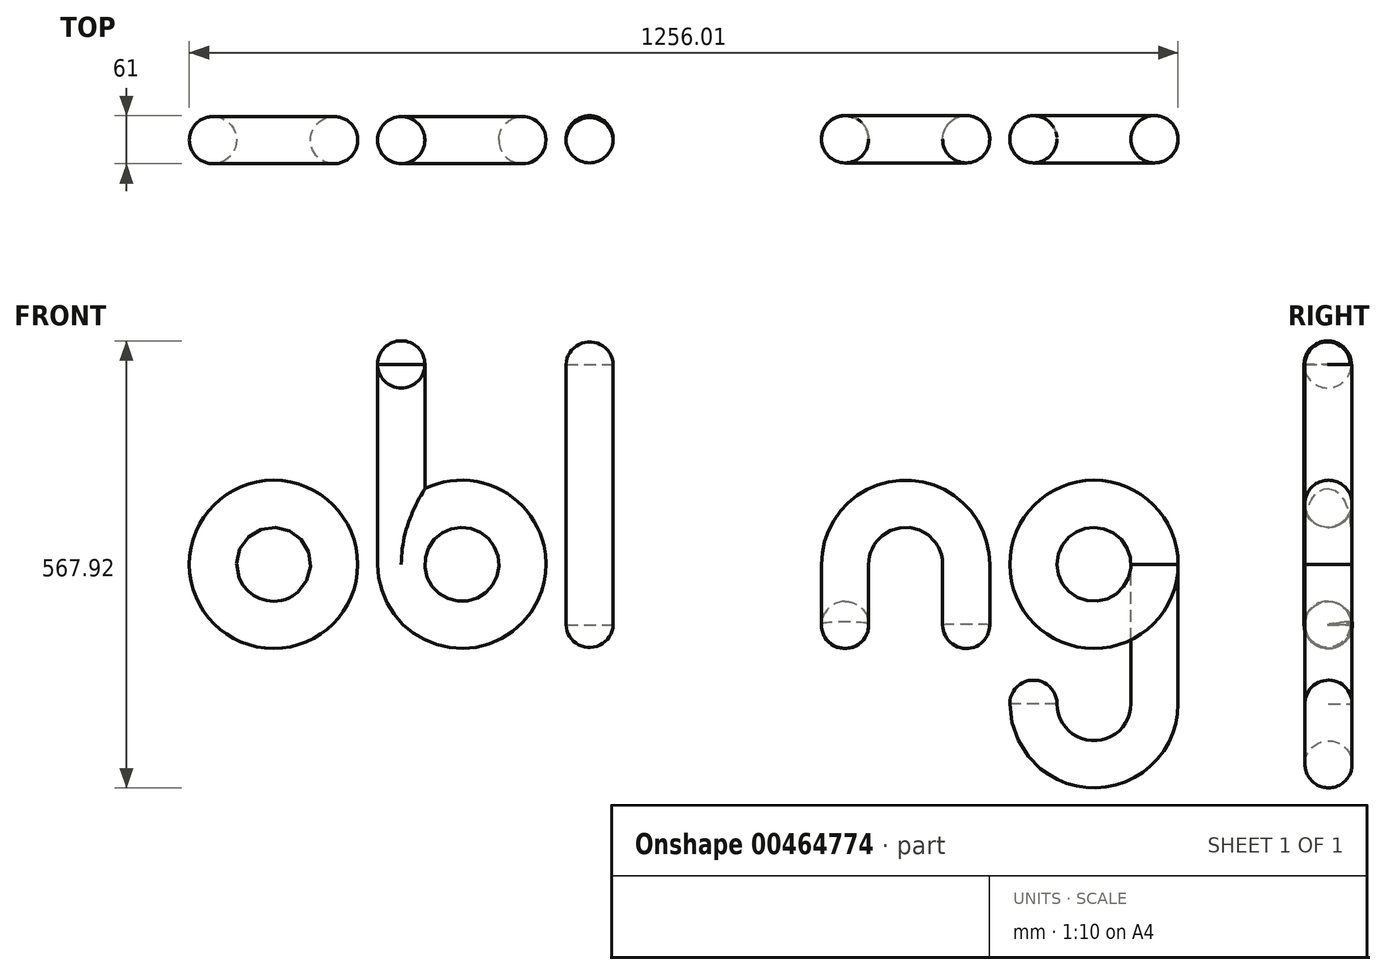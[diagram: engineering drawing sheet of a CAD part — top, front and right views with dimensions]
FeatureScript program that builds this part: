
annotation { "Feature Type Name" : "Feature", "Feature Type Description" : "" }
export const myFeature = defineFeature(function(context is Context, id is Id, definition is map)
    precondition{}
    {
        {
            var Q0;
            Q0=qCreatedBy(makeId("Top.planeOp"),FACE);
            var sketch = newSketch(context, id + "F0", { "sketchPlane" : qUnion([Q0])});
            skCircle(sketch, "E0", {"center": v(0, 0) * mm, "radius": 29.96 * mm});
            skLineSegment(sketch, "E1", {"start": v(-39.68, 0) * mm, "end": v(42.5, 0) * mm});
            skSolve(sketch);
        }
        {
            var Q0;
            {var subQ0=sQuery(id+"F0.wireOp",EDGE,"E1");var subQ1=sQuery(id+"F0.wireOp",EDGE,"E0");var subQ2=makeQuery(id+"F0.imprint","INTERSECT",VERTEX,{"disambiguationData":[OD(0.0)],"derivedFrom":[subQ1,subQ0]});Q0=makeQuery(id+"F0.imprint","IMPRINT",FACE,{"disambiguationData":[TD([[makeQuery(id+"F0.imprint","IMPRINT",EDGE,{"disambiguationData":[TD([[subQ2,1.0]])],"derivedFrom":subQ1}),1.0]])]});}
            var Q1;
            Q1=sQuery(id+"F0.wireOp",EDGE,"E1");
            revolve(context, id + "F1", {"entities" : qUnion([Q0]), "axis" : qUnion([Q1]), "revolveType" : RevolveType.FULL});
        }
        {
            var Q0;
            {var subQ0=sQuery(id+"F0.wireOp",EDGE,"E1");var subQ1=sQuery(id+"F0.wireOp",EDGE,"E0");var subQ2=makeQuery(id+"F0.imprint","INTERSECT",VERTEX,{"disambiguationData":[OD(0.0)],"derivedFrom":[subQ1,subQ0]});Q0=makeQuery(id+"F0.imprint","IMPRINT",FACE,{"disambiguationData":[TD([[makeQuery(id+"F0.imprint","IMPRINT",EDGE,{"disambiguationData":[TD([[subQ2,1.0]])],"derivedFrom":subQ1}),1.0]])]});}
            var Q1;
            {var subQ0=sQuery(id+"F0.wireOp",EDGE,"E1");var subQ1=sQuery(id+"F0.wireOp",EDGE,"E0");var subQ2=makeQuery(id+"F0.imprint","INTERSECT",VERTEX,{"disambiguationData":[OD(0.0)],"derivedFrom":[subQ1,subQ0]});Q1=makeQuery(id+"F0.imprint","IMPRINT",FACE,{"disambiguationData":[TD([[makeQuery(id+"F0.imprint","IMPRINT",EDGE,{"disambiguationData":[TD([[subQ2,-1.0]])],"derivedFrom":subQ1}),1.0]])]});}
            extrude(context, id + "F2", {"entities" : qUnion([Q0, Q1]), "oppositeDirection" : true, "depth" : 254 * mm});
        }
        {
            var Q0;
            Q0=makeQuery(id+"F2.opExtrude","CAP_FACE",FACE,{"disambiguationData":[OSD([sQuery(id+"F0.wireOp",EDGE,"E0")])],"isStart":false});
            var sketch = newSketch(context, id + "F3", { "sketchPlane" : qUnion([Q0])});
            skLineSegment(sketch, "E2", {"start": v(76.95, 56.53) * mm, "end": v(76.95, -45.65) * mm});
            skLineSegment(sketch, "E3", {"start": v(-42.66, 53.66) * mm, "end": v(-42.66, -48.45) * mm});
            skCircle(sketch, "E4", {"center": v(-85.32, 0) * mm, "radius": 29.96 * mm});
            skLineSegment(sketch, "E5", {"start": v(-162.27, 52.41) * mm, "end": v(-162.27, -53.8) * mm});
            skCircle(sketch, "E6", {"center": v(153.9, 0) * mm, "radius": 29.96 * mm});
            skLineSegment(sketch, "E7", {"start": v(-185.14, -1.07) * mm, "end": v(1029.73, -1.07) * mm});
            skLineSegment(sketch, "E8", {"start": v(196.56, 55.6) * mm, "end": v(196.56, -44.98) * mm});
            skCircle(sketch, "E9", {"center": v(239.22, -1.07) * mm, "radius": 29.96 * mm});
            skLineSegment(sketch, "E10", {"start": v(281.88, 60.27) * mm, "end": v(281.88, -45.7) * mm});
            skCircle(sketch, "E11", {"center": v(324.54, -1.07) * mm, "radius": 29.96 * mm});
            skLineSegment(sketch, "E12", {"start": v(401.5, -44.95) * mm, "end": v(401.5, 59.66) * mm});
            skCircle(sketch, "E13", {"center": v(478.44, -1.07) * mm, "radius": 29.96 * mm});
            skCircle(sketch, "E14", {"center": v(563.76, -1.07) * mm, "radius": 29.96 * mm});
            skCircle(sketch, "E15", {"center": v(717.66, -1.07) * mm, "radius": 29.96 * mm});
            skCircle(sketch, "E16", {"center": v(802.98, -1.07) * mm, "radius": 29.96 * mm});
            skLineSegment(sketch, "E17", {"start": v(521.1, -41.28) * mm, "end": v(521.1, 41.77) * mm});
            skLineSegment(sketch, "E18", {"start": v(640.7, -43.14) * mm, "end": v(640.7, 48.3) * mm});
            skLineSegment(sketch, "E19", {"start": v(760.32, -41.28) * mm, "end": v(760.32, 42.7) * mm});
            skLineSegment(sketch, "E20", {"start": v(879.93, -58.07) * mm, "end": v(879.93, 33.38) * mm});
            skCircle(sketch, "E21", {"center": v(956.87, -1.07) * mm, "radius": 29.96 * mm});
            skSolve(sketch);
        }
        {
            var Q0;
            Q0=makeQuery(id+"F3.imprint","IMPRINT",FACE,{"disambiguationData":[TD([[makeQuery(id+"F3.imprint","IMPRINT",EDGE,{"derivedFrom":makeQuery(id+"F2.opExtrude","CAP_EDGE",EDGE,{"disambiguationData":[OSD([sQuery(id+"F0.wireOp",EDGE,"E0")])],"isStart":false})}),-1.0]])]});
            var Q1;
            Q1=sQuery(id+"F3.wireOp",EDGE,"E2");
            revolve(context, id + "F4", {"operationType" : NewBodyOperationType.ADD, "entities" : qUnion([Q0]), "axis" : qUnion([Q1]), "revolveType" : RevolveType.FULL});
        }
        {
            var Q0;
            Q0=makeQuery(id+"F1.opRevolve","SWEPT_BODY",BODY,{"disambiguationData":[OSD([sQuery(id+"F0.wireOp",EDGE,"E0"),sQuery(id+"F0.wireOp",EDGE,"E1")])]});
            transform(context, id + "F5", {"entities" : qUnion([Q0]), "transformType" : TransformType.COPY});
        }
        {
            var Q0;
            Q0=makeQuery(id+"F5.opPattern","COPY",BODY,{"derivedFrom":makeQuery(id+"F1.opRevolve","SWEPT_BODY",BODY,{"disambiguationData":[OSD([sQuery(id+"F0.wireOp",EDGE,"E0"),sQuery(id+"F0.wireOp",EDGE,"E1")])]}),"instanceName":"1"});
            deleteBodies(context, id + "F6", {"entities" : qUnion([Q0])});
        }
        {
            var Q0;
            Q0=makeQuery(id+"F3.imprint","IMPRINT",FACE,{"disambiguationData":[TD([[makeQuery(id+"F3.imprint","IMPRINT",EDGE,{"derivedFrom":sQuery(id+"F3.wireOp",EDGE,"E4")}),1.0]])]});
            var Q1;
            Q1=sQuery(id+"F3.wireOp",EDGE,"E5");
            revolve(context, id + "F7", {"entities" : qUnion([Q0]), "axis" : qUnion([Q1]), "revolveType" : RevolveType.FULL});
        }
        {
            var Q0;
            Q0=makeQuery(id+"F3.imprint","IMPRINT",FACE,{"disambiguationData":[TD([[makeQuery(id+"F3.imprint","IMPRINT",EDGE,{"derivedFrom":sQuery(id+"F3.wireOp",EDGE,"E9")}),1.0]])]});
            extrude(context, id + "F8", {"entities" : qUnion([Q0]), "depth" : 76.95 * mm, "hasSecondDirection" : true, "secondDirectionOppositeDirection" : true, "secondDirectionDepth" : 254 * mm});
        }
        {
            var Q0;
            Q0=makeQuery(id+"F8.opExtrude","CAP_FACE",FACE,{"disambiguationData":[OSD([sQuery(id+"F3.wireOp",EDGE,"E9")])],"isStart":true});
            var sketch = newSketch(context, id + "F9", { "sketchPlane" : qUnion([Q0])});
            skLineSegment(sketch, "E22", {"start": v(202.9, -0.23) * mm, "end": v(276.28, -0.23) * mm});
            skSolve(sketch);
        }
        {
            var Q0;
            {var subQ0=sQuery(id+"F9.wireOp",EDGE,"E22");var subQ1=makeQuery(id+"F8.opExtrude","CAP_EDGE",EDGE,{"disambiguationData":[OSD([sQuery(id+"F3.wireOp",EDGE,"E9")])],"isStart":true});var subQ2=makeQuery(id+"F9.imprint","INTERSECT",VERTEX,{"disambiguationData":[OD(0.0)],"derivedFrom":[subQ1,subQ0]});Q0=makeQuery(id+"F9.imprint","IMPRINT",FACE,{"disambiguationData":[TD([[makeQuery(id+"F9.imprint","IMPRINT",EDGE,{"disambiguationData":[TD([[subQ2,-1.0]])],"derivedFrom":subQ0}),-1.0]])]});}
            var Q1;
            Q1=sQuery(id+"F9.wireOp",EDGE,"E22");
            revolve(context, id + "F10", {"operationType" : NewBodyOperationType.ADD, "entities" : qUnion([Q0]), "axis" : qUnion([Q1]), "revolveType" : RevolveType.FULL});
        }
        {
            var Q0;
            Q0=makeQuery(id+"F8.opExtrude","CAP_FACE",FACE,{"disambiguationData":[OSD([sQuery(id+"F3.wireOp",EDGE,"E9")])],"isStart":false});
            var sketch = newSketch(context, id + "F11", { "sketchPlane" : qUnion([Q0])});
            skLineSegment(sketch, "E23", {"start": v(206.6, 0.27) * mm, "end": v(272.66, 0.27) * mm});
            skSolve(sketch);
        }
        {
            var Q0;
            {var subQ0=sQuery(id+"F11.wireOp",EDGE,"E23");var subQ1=makeQuery(id+"F8.opExtrude","CAP_EDGE",EDGE,{"disambiguationData":[OSD([sQuery(id+"F3.wireOp",EDGE,"E9")])],"isStart":false});var subQ2=makeQuery(id+"F11.imprint","INTERSECT",VERTEX,{"disambiguationData":[OD(0.0)],"derivedFrom":[subQ1,subQ0]});Q0=makeQuery(id+"F11.imprint","IMPRINT",FACE,{"disambiguationData":[TD([[makeQuery(id+"F11.imprint","IMPRINT",EDGE,{"disambiguationData":[TD([[subQ2,-1.0]])],"derivedFrom":subQ0}),1.0]])]});}
            var Q1;
            Q1=sQuery(id+"F11.wireOp",EDGE,"E23");
            revolve(context, id + "F12", {"operationType" : NewBodyOperationType.ADD, "entities" : qUnion([Q0]), "axis" : qUnion([Q1]), "revolveType" : RevolveType.FULL});
        }
        {
            var Q0;
            Q0=sQuery(id+"F3.wireOp",EDGE,"E11");
            var Q1;
            Q1=sQuery(id+"F3.wireOp",EDGE,"E12");
            revolve(context, id + "F13", {"bodyType" : ToolBodyType.SURFACE, "surfaceEntities" : qUnion([Q0]), "axis" : qUnion([Q1]), "revolveType" : RevolveType.FULL});
        }
        {
            var Q0;
            {var subQ0=sQuery(id+"F3.wireOp",EDGE,"E14");var subQ1=sQuery(id+"F3.wireOp",EDGE,"E7");var subQ2=makeQuery(id+"F3.imprint","INTERSECT",VERTEX,{"disambiguationData":[OD(0.0)],"derivedFrom":[subQ1,subQ0]});Q0=makeQuery(id+"F3.imprint","IMPRINT",FACE,{"disambiguationData":[TD([[makeQuery(id+"F3.imprint","IMPRINT",EDGE,{"disambiguationData":[TD([[subQ2,-1.0]])],"derivedFrom":subQ1}),-1.0]])]});}
            var Q1;
            {var subQ0=sQuery(id+"F3.wireOp",EDGE,"E14");var subQ1=sQuery(id+"F3.wireOp",EDGE,"E7");var subQ2=makeQuery(id+"F3.imprint","INTERSECT",VERTEX,{"disambiguationData":[OD(0.0)],"derivedFrom":[subQ1,subQ0]});Q1=makeQuery(id+"F3.imprint","IMPRINT",FACE,{"disambiguationData":[TD([[makeQuery(id+"F3.imprint","IMPRINT",EDGE,{"disambiguationData":[TD([[subQ2,-1.0]])],"derivedFrom":subQ1}),1.0]])]});}
            var Q2;
            Q2=sQuery(id+"F3.wireOp",EDGE,"E18");
            revolve(context, id + "F14", {"entities" : qUnion([Q0, Q1]), "axis" : qUnion([Q2]), "revolveType" : RevolveType.ONE_DIRECTION, "oppositeDirection" : true, "angle" : 180 * degree});
        }
        {
            var Q0;
            {var subQ0=sQuery(id+"F3.wireOp",EDGE,"E14");var subQ1=sQuery(id+"F3.wireOp",EDGE,"E7");var subQ2=makeQuery(id+"F3.imprint","INTERSECT",VERTEX,{"disambiguationData":[OD(0.0)],"derivedFrom":[subQ1,subQ0]});Q0=makeQuery(id+"F3.imprint","IMPRINT",FACE,{"disambiguationData":[TD([[makeQuery(id+"F3.imprint","IMPRINT",EDGE,{"disambiguationData":[TD([[subQ2,-1.0]])],"derivedFrom":subQ1}),-1.0]])]});}
            var Q1;
            {var subQ0=sQuery(id+"F3.wireOp",EDGE,"E14");var subQ1=sQuery(id+"F3.wireOp",EDGE,"E7");var subQ2=makeQuery(id+"F3.imprint","INTERSECT",VERTEX,{"disambiguationData":[OD(0.0)],"derivedFrom":[subQ1,subQ0]});Q1=makeQuery(id+"F3.imprint","IMPRINT",FACE,{"disambiguationData":[TD([[makeQuery(id+"F3.imprint","IMPRINT",EDGE,{"disambiguationData":[TD([[subQ2,-1.0]])],"derivedFrom":subQ1}),1.0]])]});}
            extrude(context, id + "F15", {"entities" : qUnion([Q0, Q1]), "operationType" : NewBodyOperationType.ADD, "depth" : 76.96 * mm});
        }
        {
            var Q0;
            Q0=makeQuery(id+"F15.opExtrude","CAP_FACE",FACE,{"disambiguationData":[OSD([sQuery(id+"F3.wireOp",EDGE,"E14")])],"isStart":false});
            var sketch = newSketch(context, id + "F16", { "sketchPlane" : qUnion([Q0])});
            skLineSegment(sketch, "E24", {"start": v(533.8, -1.22) * mm, "end": v(593.72, -1.22) * mm});
            skSolve(sketch);
        }
        {
            var Q0;
            {var subQ0=sQuery(id+"F16.wireOp",EDGE,"E24");Q0=makeQuery(id+"F16.imprint","IMPRINT",FACE,{"disambiguationData":[TD([[makeQuery(id+"F16.imprint","IMPRINT",EDGE,{"derivedFrom":subQ0}),1.0]])]});}
            var Q1;
            Q1=sQuery(id+"F16.wireOp",EDGE,"E24");
            revolve(context, id + "F17", {"operationType" : NewBodyOperationType.ADD, "entities" : qUnion([Q0]), "axis" : qUnion([Q1]), "revolveType" : RevolveType.FULL});
        }
        {
            var Q0;
            {var subQ0=sQuery(id+"F3.wireOp",EDGE,"E15");var subQ1=sQuery(id+"F3.wireOp",EDGE,"E7");var subQ2=makeQuery(id+"F3.imprint","INTERSECT",VERTEX,{"disambiguationData":[OD(0.0)],"derivedFrom":[subQ1,subQ0]});Q0=makeQuery(id+"F3.imprint","IMPRINT",FACE,{"disambiguationData":[TD([[makeQuery(id+"F3.imprint","IMPRINT",EDGE,{"disambiguationData":[TD([[subQ2,-1.0]])],"derivedFrom":subQ1}),1.0]])]});}
            var Q1;
            {var subQ0=sQuery(id+"F3.wireOp",EDGE,"E15");var subQ1=sQuery(id+"F3.wireOp",EDGE,"E7");var subQ2=makeQuery(id+"F3.imprint","INTERSECT",VERTEX,{"disambiguationData":[OD(0.0)],"derivedFrom":[subQ1,subQ0]});Q1=makeQuery(id+"F3.imprint","IMPRINT",FACE,{"disambiguationData":[TD([[makeQuery(id+"F3.imprint","IMPRINT",EDGE,{"disambiguationData":[TD([[subQ2,-1.0]])],"derivedFrom":subQ1}),-1.0]])]});}
            extrude(context, id + "F18", {"entities" : qUnion([Q0, Q1]), "operationType" : NewBodyOperationType.ADD, "depth" : 76.96 * mm});
        }
        {
            var Q0;
            Q0=makeQuery(id+"F18.opExtrude","CAP_FACE",FACE,{"disambiguationData":[OSD([sQuery(id+"F3.wireOp",EDGE,"E15")])],"isStart":false});
            var sketch = newSketch(context, id + "F19", { "sketchPlane" : qUnion([Q0])});
            skLineSegment(sketch, "E25", {"start": v(687.7, -1.09) * mm, "end": v(747.62, -1.09) * mm});
            skSolve(sketch);
        }
        {
            var Q0;
            {var subQ0=sQuery(id+"F19.wireOp",EDGE,"E25");Q0=makeQuery(id+"F19.imprint","IMPRINT",FACE,{"disambiguationData":[TD([[makeQuery(id+"F19.imprint","IMPRINT",EDGE,{"derivedFrom":subQ0}),1.0]])]});}
            var Q1;
            Q1=sQuery(id+"F19.wireOp",EDGE,"E25");
            revolve(context, id + "F20", {"operationType" : NewBodyOperationType.ADD, "entities" : qUnion([Q0]), "axis" : qUnion([Q1]), "revolveType" : RevolveType.FULL});
        }
        {
            var Q0;
            {var subQ0=sQuery(id+"F3.wireOp",EDGE,"E16");var subQ1=sQuery(id+"F3.wireOp",EDGE,"E7");var subQ2=makeQuery(id+"F3.imprint","INTERSECT",VERTEX,{"disambiguationData":[OD(0.0)],"derivedFrom":[subQ1,subQ0]});Q0=makeQuery(id+"F3.imprint","IMPRINT",FACE,{"disambiguationData":[TD([[makeQuery(id+"F3.imprint","IMPRINT",EDGE,{"disambiguationData":[TD([[subQ2,-1.0]])],"derivedFrom":subQ1}),-1.0]])]});}
            var Q1;
            {var subQ0=sQuery(id+"F3.wireOp",EDGE,"E16");var subQ1=sQuery(id+"F3.wireOp",EDGE,"E7");var subQ2=makeQuery(id+"F3.imprint","INTERSECT",VERTEX,{"disambiguationData":[OD(0.0)],"derivedFrom":[subQ1,subQ0]});Q1=makeQuery(id+"F3.imprint","IMPRINT",FACE,{"disambiguationData":[TD([[makeQuery(id+"F3.imprint","IMPRINT",EDGE,{"disambiguationData":[TD([[subQ2,-1.0]])],"derivedFrom":subQ1}),1.0]])]});}
            var Q2;
            Q2=sQuery(id+"F3.wireOp",EDGE,"E20");
            revolve(context, id + "F21", {"entities" : qUnion([Q0, Q1]), "axis" : qUnion([Q2]), "revolveType" : RevolveType.FULL});
        }
        {
            var Q0;
            {var subQ0=sQuery(id+"F3.wireOp",EDGE,"E21");var subQ1=sQuery(id+"F3.wireOp",EDGE,"E7");var subQ2=makeQuery(id+"F3.imprint","INTERSECT",VERTEX,{"disambiguationData":[OD(0.0)],"derivedFrom":[subQ1,subQ0]});Q0=makeQuery(id+"F3.imprint","IMPRINT",FACE,{"disambiguationData":[TD([[makeQuery(id+"F3.imprint","IMPRINT",EDGE,{"disambiguationData":[TD([[subQ2,-1.0]])],"derivedFrom":subQ1}),1.0]])]});}
            var Q1;
            {var subQ0=sQuery(id+"F3.wireOp",EDGE,"E21");var subQ1=sQuery(id+"F3.wireOp",EDGE,"E7");var subQ2=makeQuery(id+"F3.imprint","INTERSECT",VERTEX,{"disambiguationData":[OD(0.0)],"derivedFrom":[subQ1,subQ0]});Q1=makeQuery(id+"F3.imprint","IMPRINT",FACE,{"disambiguationData":[TD([[makeQuery(id+"F3.imprint","IMPRINT",EDGE,{"disambiguationData":[TD([[subQ2,-1.0]])],"derivedFrom":subQ1}),-1.0]])]});}
            extrude(context, id + "F22", {"entities" : qUnion([Q0, Q1]), "depth" : 177.05 * mm});
        }
        {
            var Q0;
            Q0=makeQuery(id+"F22.opExtrude","CAP_FACE",FACE,{"disambiguationData":[OSD([sQuery(id+"F3.wireOp",EDGE,"E21")])],"isStart":false});
            var sketch = newSketch(context, id + "F23", { "sketchPlane" : qUnion([Q0])});
            skLineSegment(sketch, "E26", {"start": v(879.93, 44.75) * mm, "end": v(879.93, -65.23) * mm});
            skSolve(sketch);
        }
        {
            var Q0;
            Q0=makeQuery(id+"F23.imprint","IMPRINT",FACE,{"disambiguationData":[TD([[makeQuery(id+"F23.imprint","IMPRINT",EDGE,{"derivedFrom":makeQuery(id+"F22.opExtrude","CAP_EDGE",EDGE,{"disambiguationData":[OSD([sQuery(id+"F3.wireOp",EDGE,"E21")])],"isStart":false})}),1.0]])]});
            var Q1;
            Q1=sQuery(id+"F23.wireOp",EDGE,"E26");
            revolve(context, id + "F24", {"operationType" : NewBodyOperationType.ADD, "entities" : qUnion([Q0]), "axis" : qUnion([Q1]), "revolveType" : RevolveType.ONE_DIRECTION, "angle" : 180 * degree});
        }
        {
            var Q0;
            Q0=makeQuery(id+"F24.opRevolve","CAP_FACE",FACE,{"disambiguationData":[OSD([sQuery(id+"F3.wireOp",EDGE,"E21")])],"isStart":false});
            var sketch = newSketch(context, id + "F25", { "sketchPlane" : qUnion([Q0])});
            skLineSegment(sketch, "E27", {"start": v(773.02, 1) * mm, "end": v(832.94, 1) * mm});
            skSolve(sketch);
        }
        {
            var Q0;
            {var subQ0=sQuery(id+"F3.wireOp",EDGE,"E16");var subQ1=sQuery(id+"F3.wireOp",EDGE,"E7");var subQ2=makeQuery(id+"F3.imprint","INTERSECT",VERTEX,{"disambiguationData":[OD(0.0)],"derivedFrom":[subQ1,subQ0]});Q0=makeQuery(id+"F3.imprint","IMPRINT",FACE,{"disambiguationData":[TD([[makeQuery(id+"F3.imprint","IMPRINT",EDGE,{"disambiguationData":[TD([[subQ2,-1.0]])],"derivedFrom":subQ1}),1.0]])]});}
            var Q1;
            Q1=sQuery(id+"F3.wireOp",EDGE,"E7");
            revolve(context, id + "F26", {"entities" : qUnion([Q0]), "axis" : qUnion([Q1]), "revolveType" : RevolveType.FULL});
        }
        {
            var Q0;
            {var subQ0=sQuery(id+"F25.wireOp",EDGE,"E27");Q0=makeQuery(id+"F25.imprint","IMPRINT",FACE,{"disambiguationData":[TD([[makeQuery(id+"F25.imprint","IMPRINT",EDGE,{"derivedFrom":subQ0}),-1.0]])]});}
            var Q1;
            Q1=sQuery(id+"F25.wireOp",EDGE,"E27");
            revolve(context, id + "F27", {"operationType" : NewBodyOperationType.ADD, "entities" : qUnion([Q0]), "axis" : qUnion([Q1]), "revolveType" : RevolveType.FULL});
        }
        {
            var Q0;
            Q0=makeQuery(id+"F26.opRevolve","SWEPT_BODY",BODY,{"disambiguationData":[OSD([sQuery(id+"F3.wireOp",EDGE,"E7"),sQuery(id+"F3.wireOp",EDGE,"E16")])]});
            deleteBodies(context, id + "F28", {"entities" : qUnion([Q0])});
        }
    });
